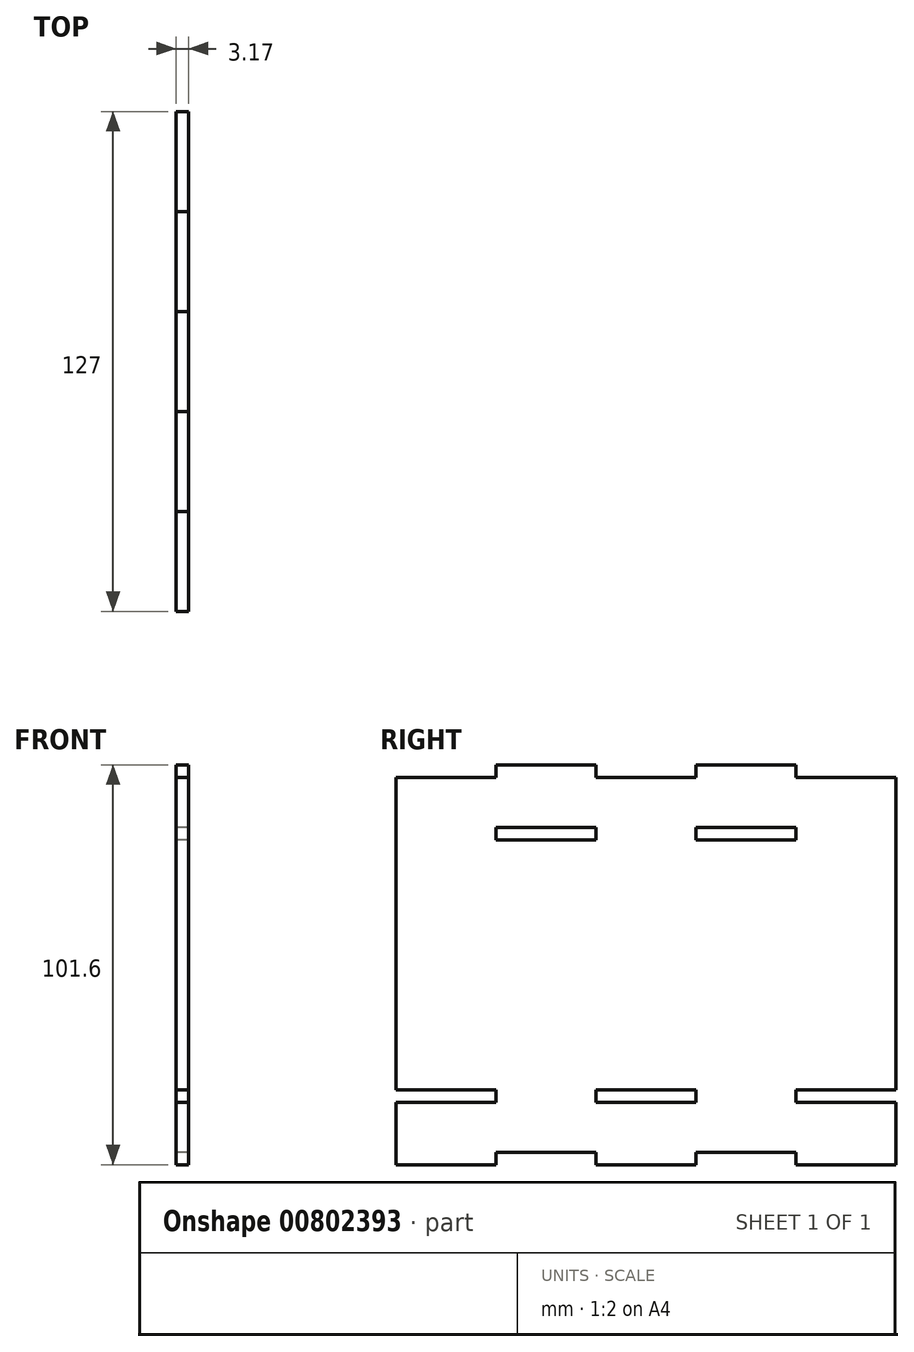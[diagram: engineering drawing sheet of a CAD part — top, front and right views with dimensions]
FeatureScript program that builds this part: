
annotation { "Feature Type Name" : "Feature", "Feature Type Description" : "" }
export const myFeature = defineFeature(function(context is Context, id is Id, definition is map)
    precondition{}
    {
        {
            var Q0;
            Q0=qCreatedBy(makeId("Right.planeOp"),FACE);
            var sketch = newSketch(context, id + "F0", { "sketchPlane" : qUnion([Q0])});
            skLineSegment(sketch, "E0.bottom", {"start": v(0, 0) * mm, "end": v(127, 0) * mm});
            skLineSegment(sketch, "E0.top", {"start": v(0, 101.6) * mm, "end": v(127, 101.6) * mm});
            skLineSegment(sketch, "E0.left", {"start": v(0, 0) * mm, "end": v(0, 101.6) * mm});
            skLineSegment(sketch, "E0.right", {"start": v(127, 0) * mm, "end": v(127, 101.6) * mm});
            skLineSegment(sketch, "E1", {"start": v(0, 0) * mm, "end": v(25.4, 0) * mm});
            skLineSegment(sketch, "E2.bottom", {"start": v(25.4, 0) * mm, "end": v(50.8, 0) * mm});
            skLineSegment(sketch, "E2.top", {"start": v(25.4, 3.18) * mm, "end": v(50.8, 3.18) * mm});
            skLineSegment(sketch, "E2.left", {"start": v(25.4, 0) * mm, "end": v(25.4, 3.17) * mm});
            skLineSegment(sketch, "E2.right", {"start": v(50.8, 0) * mm, "end": v(50.8, 3.18) * mm});
            skLineSegment(sketch, "E3", {"start": v(63.5, 0) * mm, "end": v(63.5, 101.6) * mm, "construction": true});
            skLineSegment(sketch, "E4", {"start": v(0, 50.8) * mm, "end": v(127, 50.8) * mm, "construction": true});
            skLineSegment(sketch, "E5.MirrorCS", {"start": v(101.6, 3.18) * mm, "end": v(76.2, 3.18) * mm});
            skLineSegment(sketch, "E6.MirrorCS", {"start": v(101.6, 0) * mm, "end": v(76.2, 0) * mm});
            skLineSegment(sketch, "E7.MirrorCS", {"start": v(76.2, 0) * mm, "end": v(76.2, 3.18) * mm});
            skLineSegment(sketch, "E8.MirrorCS", {"start": v(101.6, 0) * mm, "end": v(101.6, 3.17) * mm});
            skLineSegment(sketch, "E9.MirrorCS", {"start": v(25.4, 98.42) * mm, "end": v(50.8, 98.42) * mm});
            skLineSegment(sketch, "E10.MirrorCS", {"start": v(101.6, 98.42) * mm, "end": v(76.2, 98.42) * mm});
            skLineSegment(sketch, "E11.MirrorCS", {"start": v(101.6, 101.6) * mm, "end": v(76.2, 101.6) * mm});
            skLineSegment(sketch, "E12.MirrorCS", {"start": v(25.4, 101.6) * mm, "end": v(50.8, 101.6) * mm});
            skLineSegment(sketch, "E13.MirrorCS", {"start": v(101.6, 101.6) * mm, "end": v(101.6, 98.42) * mm});
            skLineSegment(sketch, "E14.MirrorCS", {"start": v(76.2, 101.6) * mm, "end": v(76.2, 98.42) * mm});
            skLineSegment(sketch, "E15.MirrorCS", {"start": v(50.8, 101.6) * mm, "end": v(50.8, 98.42) * mm});
            skLineSegment(sketch, "E16.MirrorCS", {"start": v(25.4, 101.6) * mm, "end": v(25.4, 98.42) * mm});
            skLineSegment(sketch, "E17", {"start": v(0, 98.42) * mm, "end": v(127, 98.42) * mm});
            skLineSegment(sketch, "E18", {"start": v(25.4, 3.18) * mm, "end": v(25.4, 15.88) * mm, "construction": true});
            skLineSegment(sketch, "E19.bottom", {"start": v(25.4, 15.88) * mm, "end": v(0, 15.88) * mm});
            skLineSegment(sketch, "E19.top", {"start": v(25.4, 19.05) * mm, "end": v(0, 19.05) * mm});
            skLineSegment(sketch, "E19.left", {"start": v(25.4, 15.88) * mm, "end": v(25.4, 19.05) * mm});
            skLineSegment(sketch, "E19.right", {"start": v(0, 15.87) * mm, "end": v(0, 19.05) * mm});
            skLineSegment(sketch, "E20.1.0.1", {"start": v(76.2, 15.88) * mm, "end": v(76.2, 19.05) * mm});
            skLineSegment(sketch, "E20.1.0.2", {"start": v(76.2, 15.88) * mm, "end": v(50.8, 15.88) * mm});
            skLineSegment(sketch, "E20.1.0.3", {"start": v(76.2, 19.05) * mm, "end": v(50.8, 19.05) * mm});
            skLineSegment(sketch, "E20.1.0.4", {"start": v(50.8, 15.87) * mm, "end": v(50.8, 19.05) * mm});
            skLineSegment(sketch, "E20.1.0.5", {"start": v(76.2, 3.18) * mm, "end": v(76.2, 15.88) * mm, "construction": true});
            skLineSegment(sketch, "E20.2.0.1", {"start": v(127, 15.88) * mm, "end": v(127, 19.05) * mm});
            skLineSegment(sketch, "E20.2.0.2", {"start": v(127, 15.88) * mm, "end": v(101.6, 15.88) * mm});
            skLineSegment(sketch, "E20.2.0.3", {"start": v(127, 19.05) * mm, "end": v(101.6, 19.05) * mm});
            skLineSegment(sketch, "E20.2.0.4", {"start": v(101.6, 15.87) * mm, "end": v(101.6, 19.05) * mm});
            skLineSegment(sketch, "E20.2.0.5", {"start": v(127, 3.18) * mm, "end": v(127, 15.88) * mm, "construction": true});
            skLineSegment(sketch, "E20.direction1", {"start": v(0, 0) * mm, "end": v(50.8, 0) * mm, "construction": true});
            skLineSegment(sketch, "E21.MirrorCS", {"start": v(25.4, 85.72) * mm, "end": v(25.4, 82.55) * mm});
            skLineSegment(sketch, "E22.MirrorCS", {"start": v(50.8, 85.72) * mm, "end": v(50.8, 82.55) * mm});
            skLineSegment(sketch, "E23.MirrorCS", {"start": v(76.2, 85.72) * mm, "end": v(76.2, 82.55) * mm});
            skLineSegment(sketch, "E24.MirrorCS", {"start": v(101.6, 85.72) * mm, "end": v(101.6, 82.55) * mm});
            skLineSegment(sketch, "E25", {"start": v(25.4, 85.72) * mm, "end": v(50.8, 85.72) * mm});
            skLineSegment(sketch, "E26", {"start": v(50.8, 82.55) * mm, "end": v(25.4, 82.55) * mm});
            skLineSegment(sketch, "E27", {"start": v(76.2, 85.72) * mm, "end": v(101.6, 85.72) * mm});
            skLineSegment(sketch, "E28", {"start": v(101.6, 82.55) * mm, "end": v(76.2, 82.55) * mm});
            skSolve(sketch);
        }
        {
            var Q0;
            Q0=makeQuery(id+"F0.imprint","IMPRINT",FACE,{"disambiguationData":[TD([[makeQuery(id+"F0.imprint","IMPRINT",EDGE,{"derivedFrom":sQuery(id+"F0.wireOp",EDGE,"E2.top")}),1.0]])]});
            var Q1;
            Q1=makeQuery(id+"F0.imprint","IMPRINT",FACE,{"disambiguationData":[TD([[makeQuery(id+"F0.imprint","IMPRINT",EDGE,{"derivedFrom":sQuery(id+"F0.wireOp",EDGE,"E10.MirrorCS")}),-1.0]])]});
            var Q2;
            Q2=makeQuery(id+"F0.imprint","IMPRINT",FACE,{"disambiguationData":[TD([[makeQuery(id+"F0.imprint","IMPRINT",EDGE,{"derivedFrom":sQuery(id+"F0.wireOp",EDGE,"E9.MirrorCS")}),1.0]])]});
            extrude(context, id + "F1", {"entities" : qUnion([Q0, Q1, Q2]), "depth" : 3.17 * mm, "offsetDistance" : 25.4 * mm});
        }
    });
